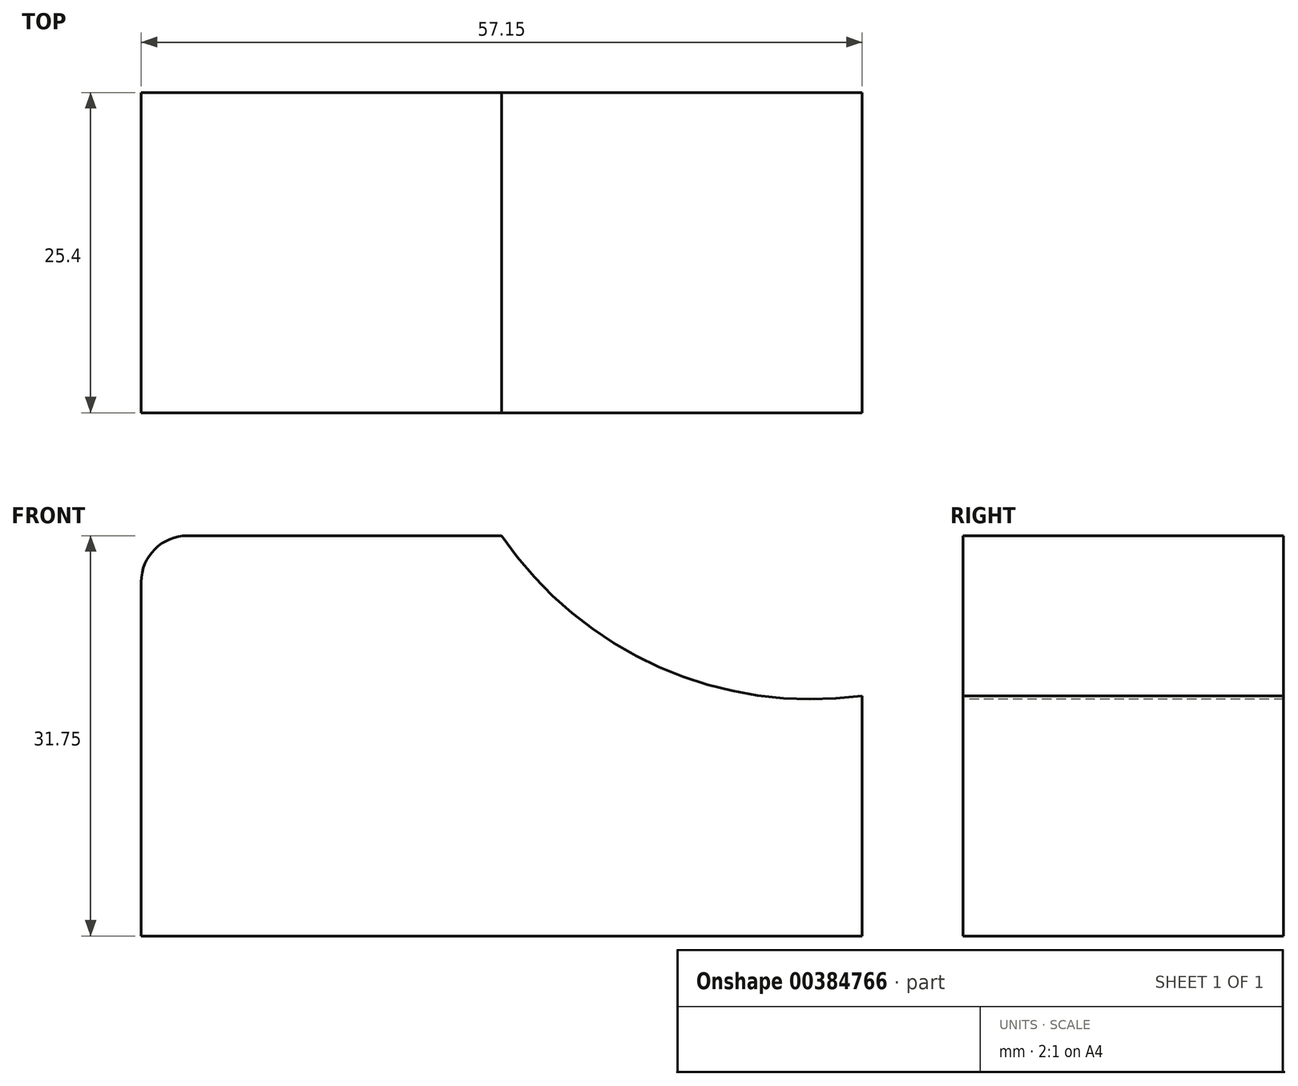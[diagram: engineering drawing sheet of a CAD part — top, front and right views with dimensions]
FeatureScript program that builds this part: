
annotation { "Feature Type Name" : "Feature", "Feature Type Description" : "" }
export const myFeature = defineFeature(function(context is Context, id is Id, definition is map)
    precondition{}
    {
        {
            var Q0;
            Q0=qCreatedBy(makeId("Front.planeOp"),FACE);
            var sketch = newSketch(context, id + "F0", { "sketchPlane" : qUnion([Q0])});
            skLineSegment(sketch, "E0", {"start": v(0, 31.75) * mm, "end": v(0, 0) * mm});
            skLineSegment(sketch, "E1", {"start": v(0, 0) * mm, "end": v(57.15, 0) * mm});
            skLineSegment(sketch, "E2", {"start": v(57.15, 0) * mm, "end": v(57.15, 31.75) * mm});
            skLineSegment(sketch, "E3", {"start": v(57.15, 31.75) * mm, "end": v(0, 31.75) * mm});
            skSolve(sketch);
        }
        {
            var Q0;
            Q0=makeQuery(id+"F0.imprint","IMPRINT",FACE,{"disambiguationData":[TD([[makeQuery(id+"F0.imprint","IMPRINT",EDGE,{"derivedFrom":sQuery(id+"F0.wireOp",EDGE,"E0")}),1.0]])]});
            extrude(context, id + "F1", {"entities" : qUnion([Q0]), "depth" : 25.4 * mm});
        }
        {
            var Q0;
            Q0=makeQuery(id+"F1.opExtrude","CAP_FACE",FACE,{"disambiguationData":[OSD([sQuery(id+"F0.wireOp",EDGE,"E0"),sQuery(id+"F0.wireOp",EDGE,"E1"),sQuery(id+"F0.wireOp",EDGE,"E2"),sQuery(id+"F0.wireOp",EDGE,"E3")])],"isStart":false});
            var sketch = newSketch(context, id + "F2", { "sketchPlane" : qUnion([Q0])});
            skArc(sketch, "E4", {"start": v(28.58, 31.75) * mm, "mid": v(41.06, 21.34) * mm, "end": v(57.15, 19.05) * mm});
            skLineSegment(sketch, "E5", {"start": v(28.57, 31.75) * mm, "end": v(57.15, 31.75) * mm});
            skLineSegment(sketch, "E6", {"start": v(57.15, 31.75) * mm, "end": v(57.15, 19.05) * mm});
            skSolve(sketch);
        }
        {
            var Q0;
            Q0=makeQuery(id+"F2.imprint","IMPRINT",FACE,{"disambiguationData":[TD([[makeQuery(id+"F2.imprint","IMPRINT",EDGE,{"derivedFrom":sQuery(id+"F2.wireOp",EDGE,"E4")}),1.0]])]});
            extrude(context, id + "F3", {"entities" : qUnion([Q0]), "operationType" : NewBodyOperationType.REMOVE, "oppositeDirection" : true, "depth" : 25.4 * mm});
        }
        {
            var Q0;
            Q0=makeQuery(id+"F1.opExtrude","SWEPT_EDGE",EDGE,{"disambiguationData":[OSD([sQuery(id+"F0.wireOp",EDGE,"E0"),sQuery(id+"F0.wireOp",EDGE,"E3")])]});
            fillet(context, id + "F4", {"entities" : qUnion([Q0]), "radius" : 3.68 * mm, "tangentPropagation" : true, "allowEdgeOverflow" : false});
        }
    });
